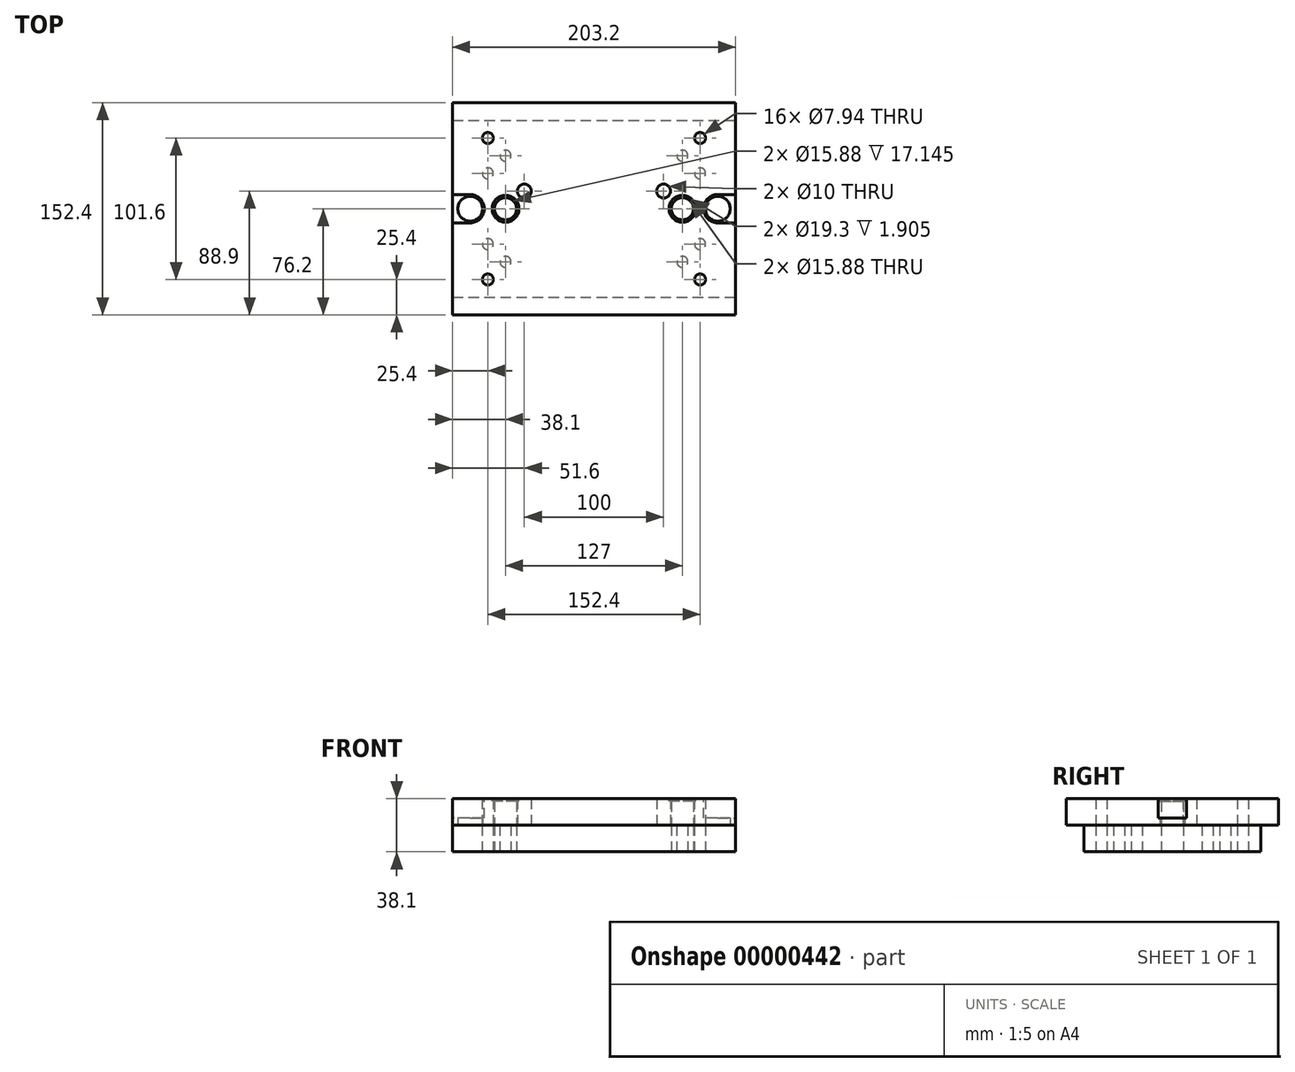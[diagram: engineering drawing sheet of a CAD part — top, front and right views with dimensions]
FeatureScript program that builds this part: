
annotation { "Feature Type Name" : "Feature", "Feature Type Description" : "" }
export const myFeature = defineFeature(function(context is Context, id is Id, definition is map)
    precondition{}
    {
        {
            var Q0;
            Q0 = qCreatedBy(makeId("Top.planeOp"), FACE);
            var sketch = newSketch(context, id + "F0", { "sketchPlane" : qUnion([Q0])});
            skLineSegment(sketch, "E0.bottom", {"start": v(0, 0) * mm, "end": v(203.2, 0) * mm});
            skLineSegment(sketch, "E0.top", {"start": v(0, 127) * mm, "end": v(203.2, 127) * mm});
            skLineSegment(sketch, "E0.left", {"start": v(0, 0) * mm, "end": v(0, 127) * mm});
            skLineSegment(sketch, "E0.right", {"start": v(203.2, 0) * mm, "end": v(203.2, 127) * mm});
            skCircle(sketch, "E1", {"center": v(38.1, 63.5) * mm, "radius": 7.94 * mm});
            skCircle(sketch, "E2", {"center": v(165.1, 63.5) * mm, "radius": 7.94 * mm});
            skCircle(sketch, "E3", {"center": v(177.8, 114.3) * mm, "radius": 3.97 * mm});
            skCircle(sketch, "E4", {"center": v(165.1, 101.6) * mm, "radius": 3.97 * mm});
            skCircle(sketch, "E5", {"center": v(177.8, 88.9) * mm, "radius": 3.97 * mm});
            skCircle(sketch, "E6", {"center": v(177.8, 38.1) * mm, "radius": 3.97 * mm});
            skCircle(sketch, "E7", {"center": v(165.1, 25.4) * mm, "radius": 3.97 * mm});
            skCircle(sketch, "E8", {"center": v(177.8, 12.7) * mm, "radius": 3.97 * mm});
            skCircle(sketch, "E9", {"center": v(25.4, 38.1) * mm, "radius": 3.97 * mm});
            skCircle(sketch, "E10", {"center": v(38.1, 25.4) * mm, "radius": 3.97 * mm});
            skCircle(sketch, "E11", {"center": v(25.4, 12.7) * mm, "radius": 3.97 * mm});
            skCircle(sketch, "E12", {"center": v(25.4, 114.3) * mm, "radius": 3.97 * mm});
            skCircle(sketch, "E13", {"center": v(38.1, 101.6) * mm, "radius": 3.97 * mm});
            skCircle(sketch, "E14", {"center": v(25.4, 88.9) * mm, "radius": 3.97 * mm});
            skSolve(sketch);
        }
        {
            var Q0;
            Q0=makeQuery(id+"F0.imprint","IMPRINT",FACE,{"disambiguationData":[TD([[makeQuery(id+"F0.imprint","IMPRINT",EDGE,{"derivedFrom":sQuery(id+"F0.wireOp",EDGE,"E0.bottom")}),1.0]])]});
            extrude(context, id + "F1", {"entities" : qUnion([Q0]), "depth" : 19.05 * mm});
        }
        {
            var Q0;
            Q0=makeQuery(id+"F1.opExtrude","CAP_FACE",FACE,{"disambiguationData":[OSD([sQuery(id+"F0.wireOp",EDGE,"E0.bottom"),sQuery(id+"F0.wireOp",EDGE,"E0.top"),sQuery(id+"F0.wireOp",EDGE,"E0.left"),sQuery(id+"F0.wireOp",EDGE,"E0.right"),sQuery(id+"F0.wireOp",EDGE,"E1"),sQuery(id+"F0.wireOp",EDGE,"E2"),sQuery(id+"F0.wireOp",EDGE,"E3"),sQuery(id+"F0.wireOp",EDGE,"E4"),sQuery(id+"F0.wireOp",EDGE,"E5"),sQuery(id+"F0.wireOp",EDGE,"E6"),sQuery(id+"F0.wireOp",EDGE,"E7"),sQuery(id+"F0.wireOp",EDGE,"E8"),sQuery(id+"F0.wireOp",EDGE,"E9"),sQuery(id+"F0.wireOp",EDGE,"E10"),sQuery(id+"F0.wireOp",EDGE,"E11"),sQuery(id+"F0.wireOp",EDGE,"E12"),sQuery(id+"F0.wireOp",EDGE,"E13"),sQuery(id+"F0.wireOp",EDGE,"E14")])],"isStart":false});
            var sketch = newSketch(context, id + "F2", { "sketchPlane" : qUnion([Q0])});
            skCircle(sketch, "E15", {"center": v(12.7, 63.5) * mm, "radius": 8.9 * mm});
            skCircle(sketch, "E16", {"center": v(190.5, 63.5) * mm, "radius": 8.9 * mm});
            skSolve(sketch);
        }
        {
            var Q0;
            {Q0=qUnion([makeQuery(id+"F2.imprint","IMPRINT",FACE,{"disambiguationData":[TD([[makeQuery(id+"F2.imprint","IMPRINT",EDGE,{"derivedFrom":sQuery(id+"F2.wireOp",EDGE,"E15")}),1.0]])]}),makeQuery(id+"F2.imprint","IMPRINT",FACE,{"disambiguationData":[TD([[makeQuery(id+"F2.imprint","IMPRINT",EDGE,{"derivedFrom":sQuery(id+"F2.wireOp",EDGE,"E16")}),1.0]])]})]);}
            extrude(context, id + "F3", {"entities" : qUnion([Q0]), "operationType" : NewBodyOperationType.ADD, "depth" : 12.7 * mm});
        }
        {
            var Q0;
            Q0=makeQuery(id+"F1.opExtrude","CAP_FACE",FACE,{"disambiguationData":[OSD([sQuery(id+"F0.wireOp",EDGE,"E0.bottom"),sQuery(id+"F0.wireOp",EDGE,"E0.top"),sQuery(id+"F0.wireOp",EDGE,"E0.left"),sQuery(id+"F0.wireOp",EDGE,"E0.right"),sQuery(id+"F0.wireOp",EDGE,"E1"),sQuery(id+"F0.wireOp",EDGE,"E2"),sQuery(id+"F0.wireOp",EDGE,"E3"),sQuery(id+"F0.wireOp",EDGE,"E4"),sQuery(id+"F0.wireOp",EDGE,"E5"),sQuery(id+"F0.wireOp",EDGE,"E6"),sQuery(id+"F0.wireOp",EDGE,"E7"),sQuery(id+"F0.wireOp",EDGE,"E8"),sQuery(id+"F0.wireOp",EDGE,"E9"),sQuery(id+"F0.wireOp",EDGE,"E10"),sQuery(id+"F0.wireOp",EDGE,"E11"),sQuery(id+"F0.wireOp",EDGE,"E12"),sQuery(id+"F0.wireOp",EDGE,"E13"),sQuery(id+"F0.wireOp",EDGE,"E14")])],"isStart":false});
            var sketch = newSketch(context, id + "F4", { "sketchPlane" : qUnion([Q0])});
            skCircle(sketch, "E17.0", {"center": v(165.1, 63.5) * mm, "radius": 7.94 * mm});
            skCircle(sketch, "E18.0", {"center": v(38.1, 63.5) * mm, "radius": 7.94 * mm});
            skCircle(sketch, "E19", {"center": v(151.6, 76.2) * mm, "radius": 5 * mm});
            skCircle(sketch, "E20", {"center": v(51.6, 76.2) * mm, "radius": 5 * mm});
            skCircle(sketch, "E21", {"center": v(101.6, 76.2) * mm, "radius": 62 * mm, "construction": true});
            skLineSegment(sketch, "E22", {"start": v(151.6, 76.2) * mm, "end": v(51.6, 76.2) * mm, "construction": true});
            skLineSegment(sketch, "E23", {"start": v(151.6, 76.2) * mm, "end": v(151.6, 170.81) * mm, "construction": true});
            skLineSegment(sketch, "E24", {"start": v(151.6, 170.81) * mm, "end": v(51.6, 170.81) * mm, "construction": true});
            skLineSegment(sketch, "E25", {"start": v(51.6, 170.81) * mm, "end": v(51.6, 76.2) * mm, "construction": true});
            skLineSegment(sketch, "E26", {"start": v(151.6, 76.2) * mm, "end": v(151.6, -66.04) * mm, "construction": true});
            skLineSegment(sketch, "E27", {"start": v(151.6, -66.04) * mm, "end": v(51.6, -66.04) * mm, "construction": true});
            skLineSegment(sketch, "E28", {"start": v(51.6, -66.04) * mm, "end": v(51.6, 76.2) * mm, "construction": true});
            skLineSegment(sketch, "E29.bottom", {"start": v(0, 139.7) * mm, "end": v(203.2, 139.7) * mm});
            skLineSegment(sketch, "E29.top", {"start": v(0, -12.7) * mm, "end": v(203.2, -12.7) * mm});
            skLineSegment(sketch, "E29.left", {"start": v(0, 139.7) * mm, "end": v(0, -12.7) * mm});
            skLineSegment(sketch, "E29.right", {"start": v(203.2, 139.7) * mm, "end": v(203.2, -12.7) * mm});
            skCircle(sketch, "E30.0", {"center": v(25.4, 114.3) * mm, "radius": 3.97 * mm});
            skCircle(sketch, "E31.0", {"center": v(25.4, 12.7) * mm, "radius": 3.97 * mm});
            skCircle(sketch, "E32.0", {"center": v(177.8, 12.7) * mm, "radius": 3.97 * mm});
            skCircle(sketch, "E33.0", {"center": v(177.8, 114.3) * mm, "radius": 3.97 * mm});
            skSolve(sketch);
        }
        {
            var Q0;
            Q0 = qSketchRegion(id + "F4", true);
            extrude(context, id + "F5", {"entities" : qUnion([Q0]), "depth" : 19.05 * mm});
        }
        {
            var Q0;
            Q0=makeQuery(id+"F5.opExtrude","CAP_FACE",FACE,{"disambiguationData":[OSD([sQuery(id+"F4.wireOp",EDGE,"f12a0b54-fa10-4c25-b158-2b599ede70d3.bottom"),sQuery(id+"F4.wireOp",EDGE,"f12a0b54-fa10-4c25-b158-2b599ede70d3.top"),sQuery(id+"F4.wireOp",EDGE,"f12a0b54-fa10-4c25-b158-2b599ede70d3.left"),sQuery(id+"F4.wireOp",EDGE,"f12a0b54-fa10-4c25-b158-2b599ede70d3.right"),sQuery(id+"F4.wireOp",EDGE,"3866d0eb-48e1-45a1-abc0-ab2e0e027100"),sQuery(id+"F4.wireOp",EDGE,"1ec41d8e-714b-4a7f-969d-bde90c60e2fc"),sQuery(id+"F4.wireOp",EDGE,"982b8139-a174-453d-ac8a-281eeaa9b839.trimOffspring"),sQuery(id+"F4.wireOp",EDGE,"ca4a6389-67b9-4db8-9802-1237c3d870ed.trimOffspring"),sQuery(id+"F4.wireOp",EDGE,"f29feec5-3bd4-4b61-902e-2eea5594b208.0"),sQuery(id+"F4.wireOp",EDGE,"333c7750-4939-4ecb-a295-466456577b6e.0"),sQuery(id+"F4.wireOp",EDGE,"E17.0"),sQuery(id+"F4.wireOp",EDGE,"73e719d1-7556-4e67-acdc-8f5e15c2634e.0"),sQuery(id+"F4.wireOp",EDGE,"639b8f68-ec1b-4da8-bea0-d3f7bcd5f7a5.0"),sQuery(id+"F4.wireOp",EDGE,"E18.0"),sQuery(id+"F4.wireOp",EDGE,"E19"),sQuery(id+"F4.wireOp",EDGE,"E20")])],"isStart":false});
            var sketch = newSketch(context, id + "F6", { "sketchPlane" : qUnion([Q0])});
            skCircle(sketch, "E34", {"center": v(38.1, 63.5) * mm, "radius": 9.65 * mm});
            skCircle(sketch, "E35", {"center": v(165.1, 63.5) * mm, "radius": 9.65 * mm});
            skSolve(sketch);
        }
        {
            var Q0;
            {var subQ0=makeQuery(id+"F6.imprint","IMPRINT",EDGE,{"derivedFrom":makeQuery(id+"F5.opExtrude","CAP_EDGE",EDGE,{"disambiguationData":[OSD([sQuery(id+"F4.wireOp",EDGE,"E17.0")])],"isStart":false})});var subQ1=makeQuery(id+"F6.imprint","IMPRINT",EDGE,{"derivedFrom":makeQuery(id+"F5.opExtrude","CAP_EDGE",EDGE,{"disambiguationData":[OSD([sQuery(id+"F4.wireOp",EDGE,"E18.0")])],"isStart":false})});Q0=qUnion([makeQuery(id+"F6.imprint","IMPRINT",FACE,{"disambiguationData":[TD([[subQ0,1.0]])]}),makeQuery(id+"F6.imprint","IMPRINT",FACE,{"disambiguationData":[TD([[subQ1,1.0]])]}),makeQuery(id+"F6.imprint","IMPRINT",FACE,{"disambiguationData":[TD([[makeQuery(id+"F6.imprint","IMPRINT",EDGE,{"derivedFrom":sQuery(id+"F6.wireOp",EDGE,"E34")}),1.0]])]}),makeQuery(id+"F6.imprint","IMPRINT",FACE,{"disambiguationData":[TD([[makeQuery(id+"F6.imprint","IMPRINT",EDGE,{"derivedFrom":sQuery(id+"F6.wireOp",EDGE,"E35")}),1.0]])]})]);}
            extrude(context, id + "F7", {"entities" : qUnion([Q0]), "operationType" : NewBodyOperationType.REMOVE, "oppositeDirection" : true, "depth" : 1.9 * mm});
        }
        {
            var Q0;
            Q0=makeQuery(id+"F6.imprint","IMPRINT",FACE,{"disambiguationData":[TD([[makeQuery(id+"F6.imprint","IMPRINT",EDGE,{"derivedFrom":sQuery(id+"F6.wireOp",EDGE,"E34")}),-1.0]])]});
            var sketch = newSketch(context, id + "F8", { "sketchPlane" : qUnion([Q0])});
            skCircle(sketch, "E36.0", {"center": v(12.7, 63.5) * mm, "radius": 8.9 * mm, "construction": true});
            skCircle(sketch, "E37.0", {"center": v(190.5, 63.5) * mm, "radius": 8.9 * mm, "construction": true});
            skArc(sketch, "E38", {"start": v(12.7, 53.34) * mm, "mid": v(22.86, 63.5) * mm, "end": v(12.7, 73.66) * mm});
            skArc(sketch, "E39", {"start": v(190.5, 73.66) * mm, "mid": v(180.34, 63.5) * mm, "end": v(190.5, 53.34) * mm});
            skLineSegment(sketch, "E40.0", {"start": v(203.2, 139.7) * mm, "end": v(203.2, -12.7) * mm, "construction": true});
            skLineSegment(sketch, "E41.0", {"start": v(0, 139.7) * mm, "end": v(0, -12.7) * mm, "construction": true});
            skLineSegment(sketch, "E42", {"start": v(12.7, 73.66) * mm, "end": v(0, 73.66) * mm});
            skLineSegment(sketch, "E43", {"start": v(0, 73.66) * mm, "end": v(0, 53.34) * mm});
            skLineSegment(sketch, "E44", {"start": v(0, 53.34) * mm, "end": v(12.7, 53.34) * mm});
            skLineSegment(sketch, "E45", {"start": v(190.5, 73.66) * mm, "end": v(203.2, 73.66) * mm});
            skLineSegment(sketch, "E46", {"start": v(203.2, 73.66) * mm, "end": v(203.2, 53.34) * mm});
            skLineSegment(sketch, "E47", {"start": v(203.2, 53.34) * mm, "end": v(190.5, 53.34) * mm});
            skSolve(sketch);
        }
        {
            var Q0;
            Q0 = qSketchRegion(id + "F8", true);
            var Q1;
            Q1 = qConstructionFilter(qBodyType(qCreatedBy(id + "F8" ,EDGE), BodyType.WIRE), ConstructionObject.NO);
            extrude(context, id + "F9", {"entities" : qUnion([Q0]), "operationType" : NewBodyOperationType.REMOVE, "surfaceEntities" : qUnion([Q1]), "oppositeDirection" : true, "depth" : 13.97 * mm});
        }
    });
